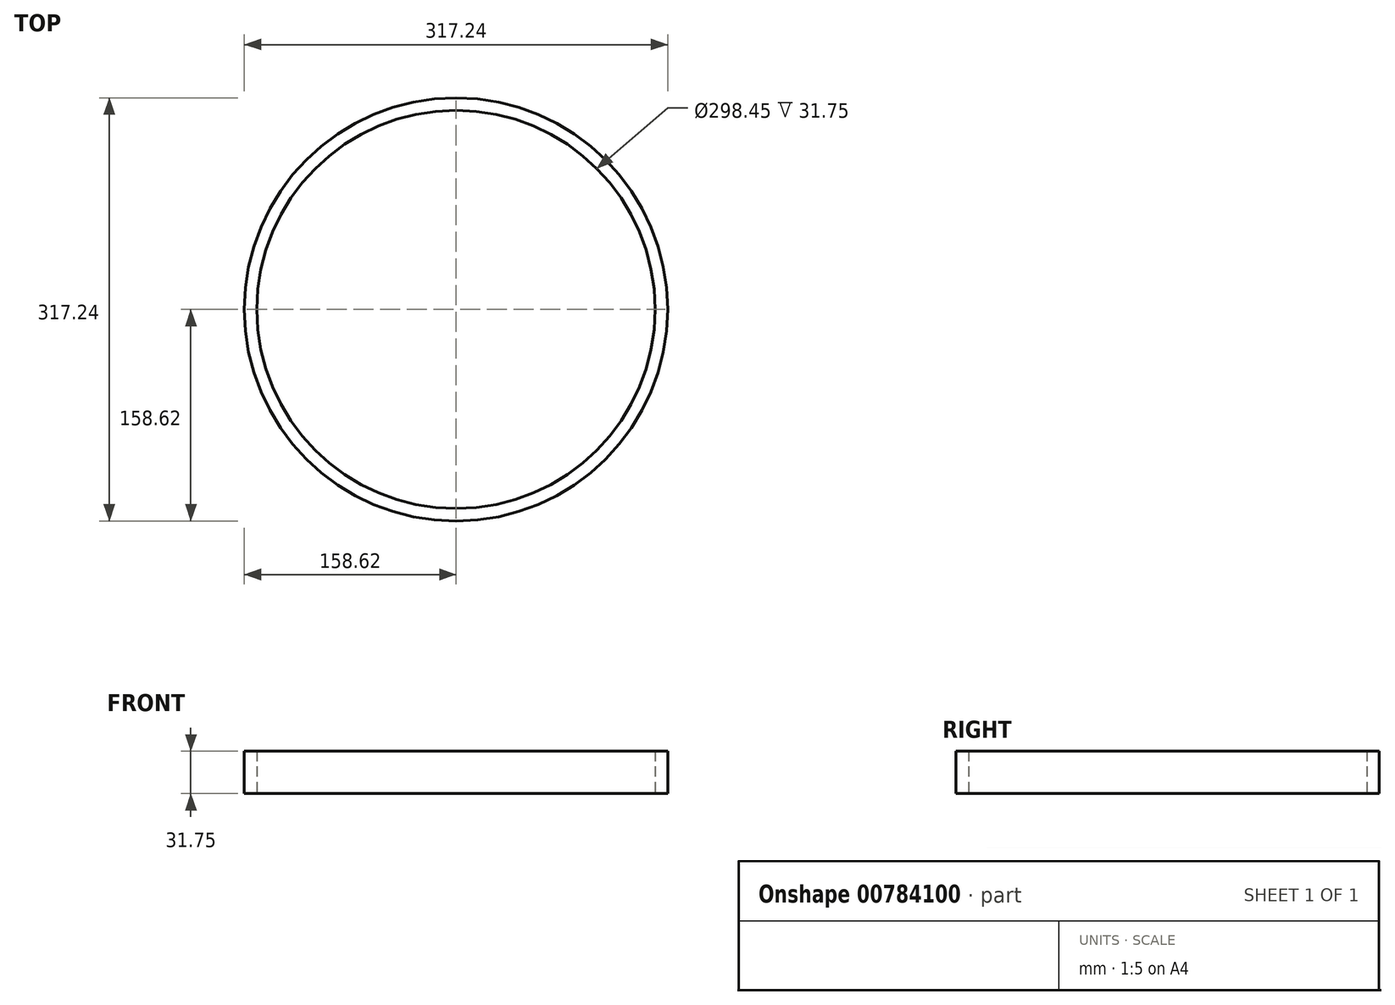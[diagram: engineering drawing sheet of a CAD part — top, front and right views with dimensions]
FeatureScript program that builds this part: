
annotation { "Feature Type Name" : "Feature", "Feature Type Description" : "" }
export const myFeature = defineFeature(function(context is Context, id is Id, definition is map)
    precondition{}
    {
        {
            var Q0;
            Q0=qCreatedBy(makeId("Top.planeOp"),FACE);
            var sketch = newSketch(context, id + "F0", { "sketchPlane" : qUnion([Q0])});
            skCircle(sketch, "E0", {"center": v(0, 0) * mm, "radius": 158.62 * mm});
            skCircle(sketch, "E1", {"center": v(0, 0) * mm, "radius": 149.23 * mm});
            skLineSegment(sketch, "E2", {"start": v(0, 0) * mm, "end": v(0, -210.77) * mm});
            skLineSegment(sketch, "E3", {"start": v(0, 0) * mm, "end": v(0, 288.22) * mm});
            skSolve(sketch);
        }
        {
            var Q0;
            Q0 = qSketchRegion(id + "F0", true);
            extrude(context, id + "F1", {"entities" : qUnion([Q0]), "depth" : 31.75 * mm, "offsetDistance" : 25.4 * mm});
        }
    });
